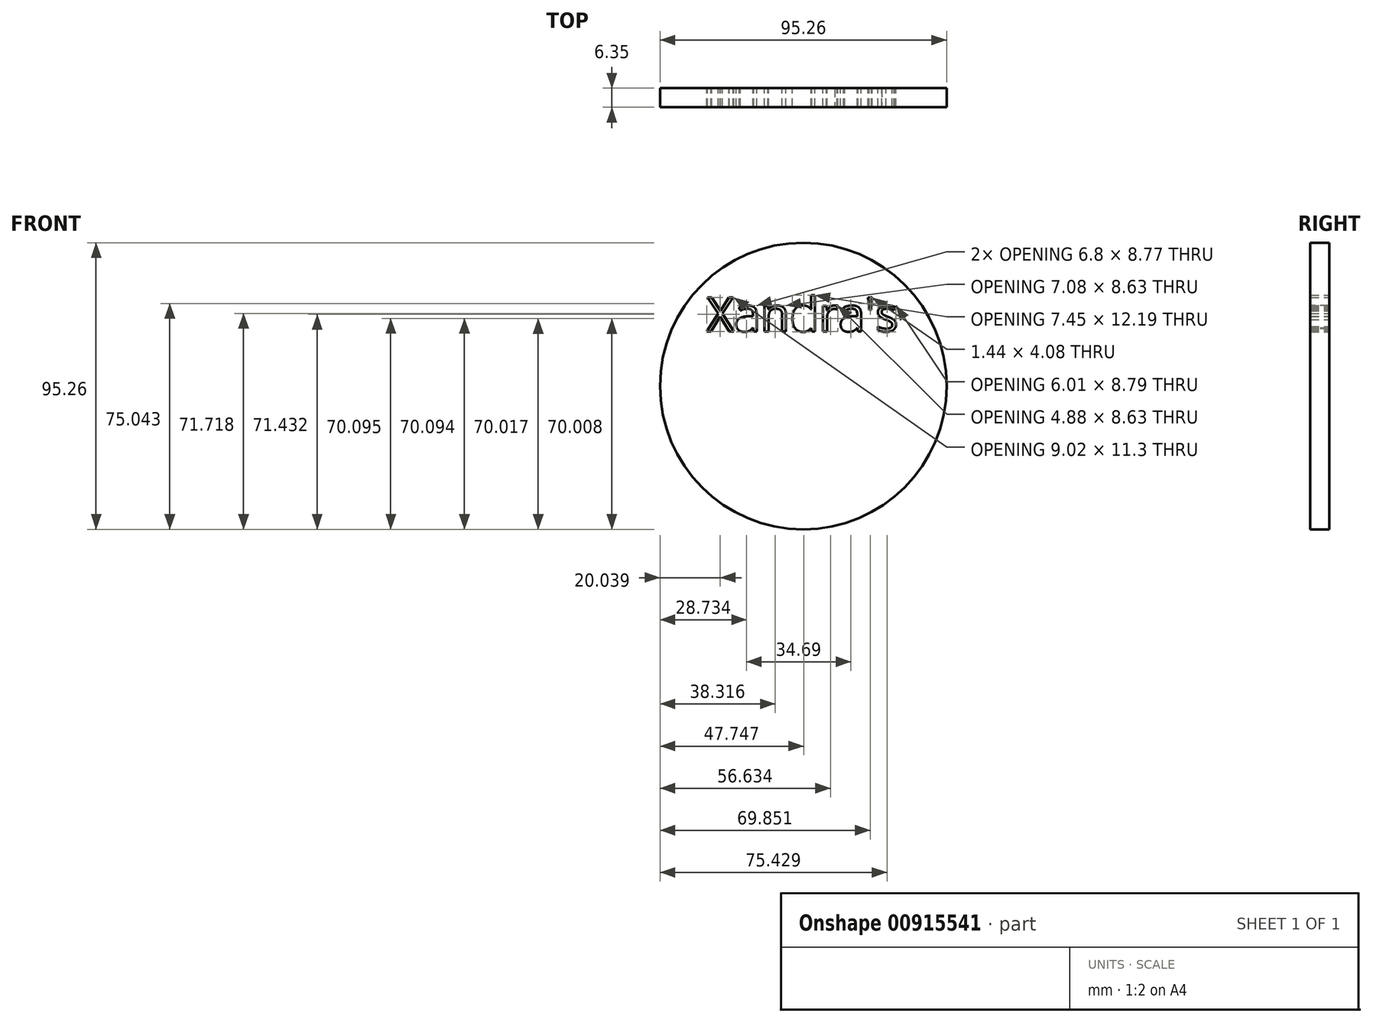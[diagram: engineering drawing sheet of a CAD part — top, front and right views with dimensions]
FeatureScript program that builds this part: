
annotation { "Feature Type Name" : "Feature", "Feature Type Description" : "" }
export const myFeature = defineFeature(function(context is Context, id is Id, definition is map)
    precondition{}
    {
        {
            var Q0;
            Q0=qCreatedBy(makeId("Front.planeOp"),FACE);
            var sketch = newSketch(context, id + "F0", { "sketchPlane" : qUnion([Q0])});
            skCircle(sketch, "E0", {"center": v(0, 0) * mm, "radius": 47.63 * mm});
            skText(sketch, "E1", { "text": "Xandra\'s", "fontName": "OpenSans-Regular.ttf"});
            const initialGuessF0  = {"E1": [-0.03216, 0.01815, 1, 0, 0.0114]};
            skSetInitialGuess(sketch, initialGuessF0);
            skSolve(sketch);
        }
        {
            var Q0;
            Q0 = qSketchRegion(id + "F0", true);
            extrude(context, id + "F1", {"entities" : qUnion([Q0]), "depth" : 6.35 * mm, "offsetDistance" : 25.4 * mm});
        }
    });
